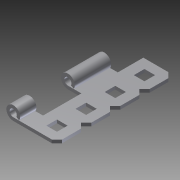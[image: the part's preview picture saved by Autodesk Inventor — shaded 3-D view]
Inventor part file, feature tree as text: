
AUTODESK INVENTOR PART (.ipt)
format: ipt  version: 2012 (Build 160160000, 160)  size: 109,568 bytes
history: native  units: in
note: dims shown in document units (in); Inventor stores cm internally (conversion verified against a paired STEP export)
features: other x2, plane x1, split x1, imported_body x1
ambient origin geometry x8: Origin, YZ Plane, XZ Plane, XY Plane, X Axis, Y Axis, Z Axis, Center Point
feature tree (5):
  other  "Cut-Extrude3"
  other  "VEX-HINGE-1 RevA1"
  plane  "Work Plane1"
  split  "Split1"
  imported_body  "Base1"
